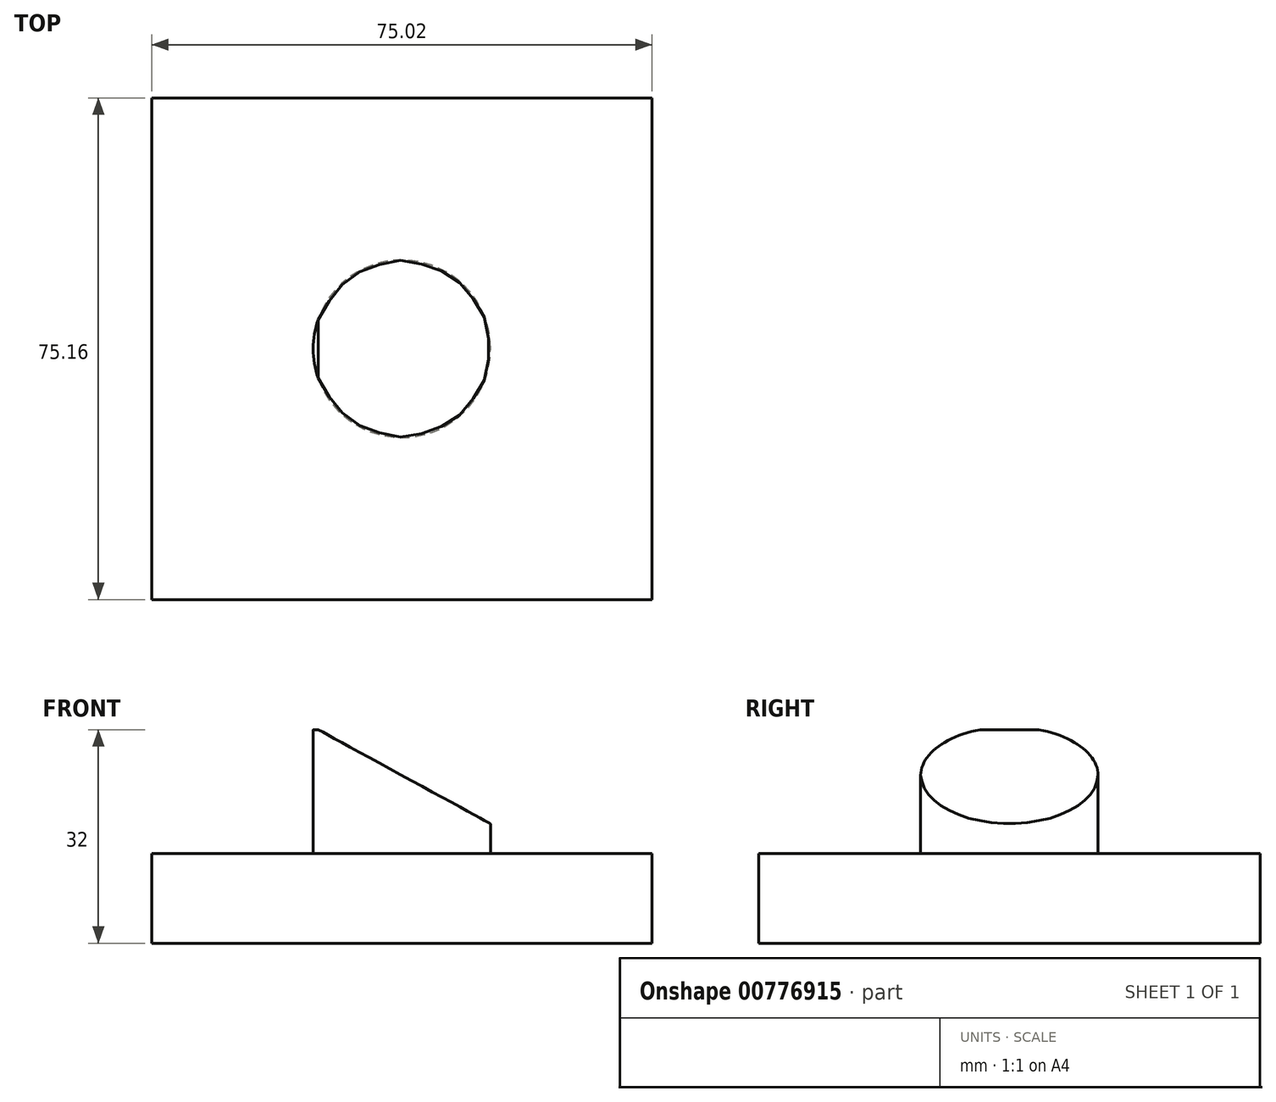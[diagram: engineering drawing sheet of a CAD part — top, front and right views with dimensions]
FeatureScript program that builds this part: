
annotation { "Feature Type Name" : "Feature", "Feature Type Description" : "" }
export const myFeature = defineFeature(function(context is Context, id is Id, definition is map)
    precondition{}
    {
        {
            var Q0;
            Q0=qCreatedBy(makeId("Top.planeOp"),FACE);
            var sketch = newSketch(context, id + "F0", { "sketchPlane" : qUnion([Q0])});
            skLineSegment(sketch, "E0.bottom", {"start": v(37.5, 37.58) * mm, "end": v(-37.5, 37.58) * mm});
            skLineSegment(sketch, "E0.top", {"start": v(37.5, -37.58) * mm, "end": v(-37.5, -37.58) * mm});
            skLineSegment(sketch, "E0.left", {"start": v(37.5, 37.58) * mm, "end": v(37.5, -37.58) * mm});
            skLineSegment(sketch, "E0.right", {"start": v(-37.5, 37.58) * mm, "end": v(-37.5, -37.58) * mm});
            skPoint(sketch, "E0.middle", {"position": v(0, 0) * mm});
            skSolve(sketch);
        }
        {
            var Q0;
            Q0=makeQuery(id+"F0.imprint","IMPRINT",FACE,{"disambiguationData":[TD([[makeQuery(id+"F0.imprint","IMPRINT",EDGE,{"derivedFrom":sQuery(id+"F0.wireOp",EDGE,"E0.bottom")}),1.0]])]});
            var Q1;
            Q1 = qSketchRegion(id + "F0", true);
            extrude(context, id + "F1", {"entities" : qUnion([Q0, Q1]), "depth" : 13.46 * mm, "offsetDistance" : 25.4 * mm});
        }
        {
            var Q0;
            Q0=makeQuery(id+"F1.opExtrude","CAP_FACE",FACE,{"disambiguationData":[OSD([sQuery(id+"F0.wireOp",EDGE,"E0.bottom"),sQuery(id+"F0.wireOp",EDGE,"E0.top"),sQuery(id+"F0.wireOp",EDGE,"E0.left"),sQuery(id+"F0.wireOp",EDGE,"E0.right")])],"isStart":false});
            var sketch = newSketch(context, id + "F2", { "sketchPlane" : qUnion([Q0])});
            skCircle(sketch, "E1", {"center": v(0, 0) * mm, "radius": 13.3 * mm});
            skSolve(sketch);
        }
        {
            var Q0;
            Q0 = qSketchRegion(id + "F2", true);
            extrude(context, id + "F3", {"entities" : qUnion([Q0]), "operationType" : NewBodyOperationType.ADD, "depth" : 18.54 * mm, "offsetDistance" : 25.4 * mm});
        }
        {
            var Q0;
            Q0=qCreatedBy(makeId("Front.planeOp"),FACE);
            var sketch = newSketch(context, id + "F4", { "sketchPlane" : qUnion([Q0])});
            skLineSegment(sketch, "E2", {"start": v(-13.61, 32.58) * mm, "end": v(14.78, 17.1) * mm});
            skLineSegment(sketch, "E3", {"start": v(14.78, 17.1) * mm, "end": v(14.78, 34.13) * mm});
            skLineSegment(sketch, "E4", {"start": v(14.78, 34.13) * mm, "end": v(-13.61, 32.58) * mm});
            skSolve(sketch);
        }
        {
            var Q0;
            Q0 = qSketchRegion(id + "F4", true);
            extrude(context, id + "F5", {"entities" : qUnion([Q0]), "operationType" : NewBodyOperationType.REMOVE, "endBound" : BoundingType.SYMMETRIC, "oppositeDirection" : true, "depth" : 42.67 * mm, "offsetDistance" : 25.4 * mm});
        }
    });
